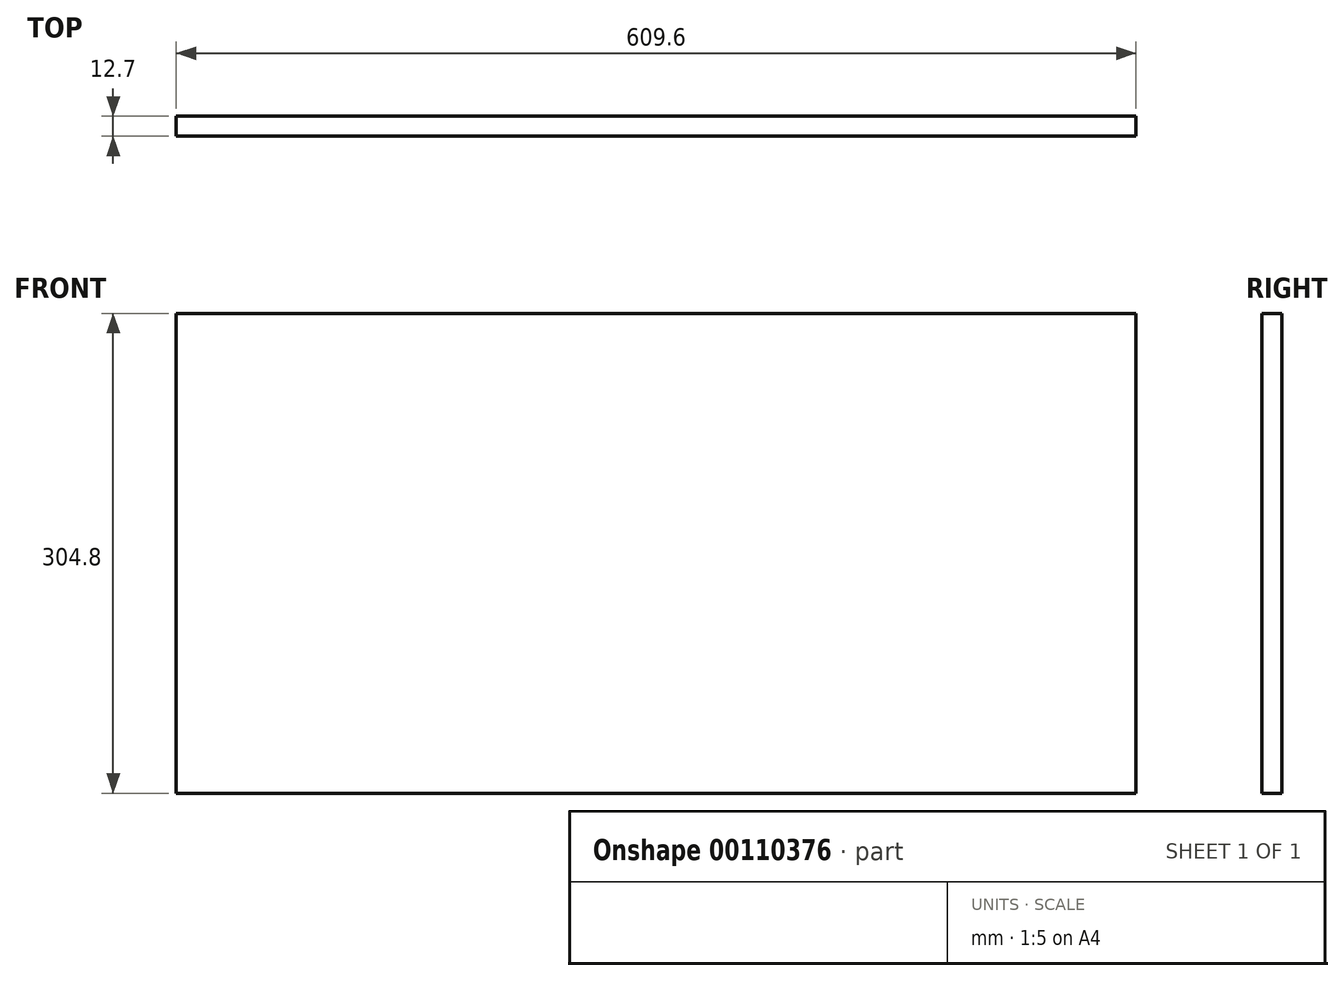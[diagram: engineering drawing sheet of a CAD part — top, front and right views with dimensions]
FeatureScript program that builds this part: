
annotation { "Feature Type Name" : "Feature", "Feature Type Description" : "" }
export const myFeature = defineFeature(function(context is Context, id is Id, definition is map)
    precondition{}
    {
        {
            var Q0;
            Q0=qCreatedBy(makeId("Front.planeOp"),FACE);
            var sketch = newSketch(context, id + "F0", { "sketchPlane" : qUnion([Q0])});
            skLineSegment(sketch, "E0.bottom", {"start": v(0, 0) * mm, "end": v(609.6, 0) * mm});
            skLineSegment(sketch, "E0.top", {"start": v(0, 304.8) * mm, "end": v(609.6, 304.8) * mm});
            skLineSegment(sketch, "E0.left", {"start": v(0, 0) * mm, "end": v(0, 304.8) * mm});
            skLineSegment(sketch, "E0.right", {"start": v(609.6, 0) * mm, "end": v(609.6, 304.8) * mm});
            skSolve(sketch);
        }
        {
            var Q0;
            Q0=makeQuery(id+"F0.imprint","IMPRINT",FACE,{"disambiguationData":[TD([[makeQuery(id+"F0.imprint","IMPRINT",EDGE,{"derivedFrom":sQuery(id+"F0.wireOp",EDGE,"E0.bottom")}),1.0]])]});
            extrude(context, id + "F1", {"entities" : qUnion([Q0]), "oppositeDirection" : true, "depth" : 12.7 * mm});
        }
    });
